# Revit family: DSP_A3-B12
name_source: partatom
category: Generic Models
revit_build: Autodesk Revit 2016 (Build: 20150220_1215(x64)
units: mm (PartAtom-declared; Revit-internal decimal feet)

## family parameters
Always vertical = Yes
Can host rebar = No
Cut with Voids When Loaded = No
Part Type = Undefined
Room Calculation Point = No
Round Connector Dimension = Use Diameter
Shared = No
Work Plane-Based = No

## types (1)
- Door
    Made by = Tolani Civil Projects cc
    Manufacturer = A3 Architects
    Offset = 100 mm  [stored 0.328084 ft]
    Panel Height = 2032 mm
    Panel Material = Meranti Wood
    Panel Thickness = 55 mm  [stored 0.180446 ft]
    Panel Width = 1200 mm
    URL = http://www.a3architects.co.za
    URL for TCP = http://www.tcpbim.co.za

note: [stored X ft] marks values corroborated as IEEE doubles in the binary element streams (Revit-internal decimal feet)

## geometry (parser evidence)
native form markers: Sweep x3
no freeform markers — native parametric forms only
